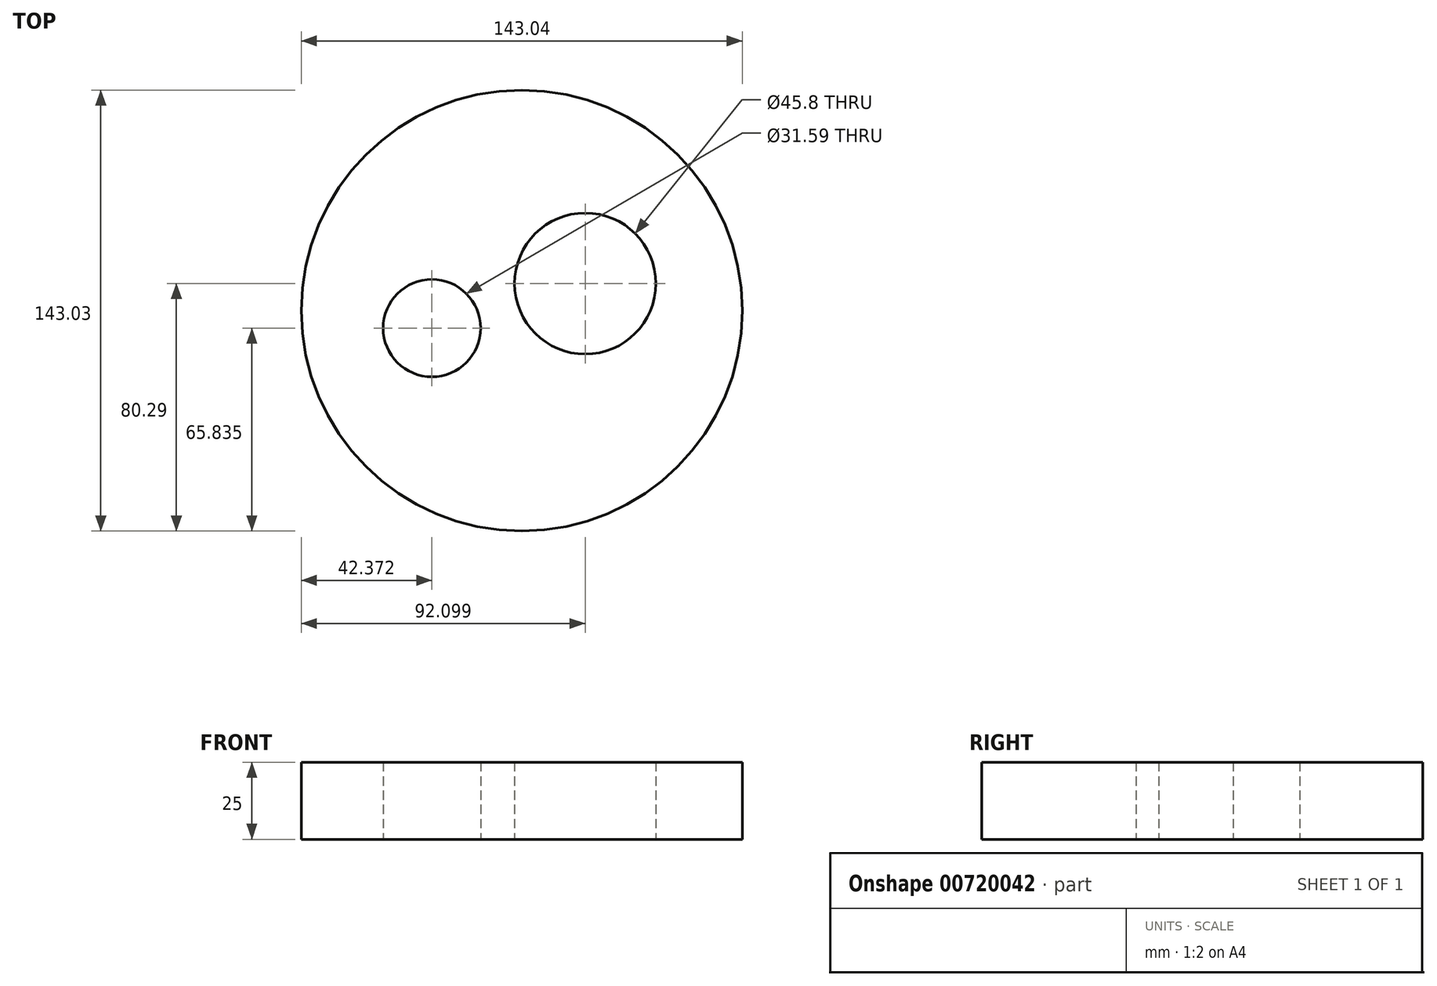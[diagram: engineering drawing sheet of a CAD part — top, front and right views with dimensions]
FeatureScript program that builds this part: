
annotation { "Feature Type Name" : "Feature", "Feature Type Description" : "" }
export const myFeature = defineFeature(function(context is Context, id is Id, definition is map)
    precondition{}
    {
        {
            var Q0;
            Q0=qCreatedBy(makeId("Top.planeOp"),FACE);
            var sketch = newSketch(context, id + "F0", { "sketchPlane" : qUnion([Q0])});
            skCircle(sketch, "E0", {"center": v(-75.75, -8.77) * mm, "radius": 71.52 * mm});
            skCircle(sketch, "E1", {"center": v(-55.17, 0) * mm, "radius": 22.9 * mm});
            skCircle(sketch, "E2", {"center": v(-104.9, -14.45) * mm, "radius": 15.8 * mm});
            skSolve(sketch);
        }
        {
            var Q0;
            Q0=makeQuery(id+"F0.imprint","IMPRINT",FACE,{"disambiguationData":[TD([[makeQuery(id+"F0.imprint","IMPRINT",EDGE,{"derivedFrom":sQuery(id+"F0.wireOp",EDGE,"E0")}),1.0]])]});
            extrude(context, id + "F1", {"entities" : qUnion([Q0]), "depth" : 25 * mm, "offsetDistance" : 25 * mm});
        }
    });
